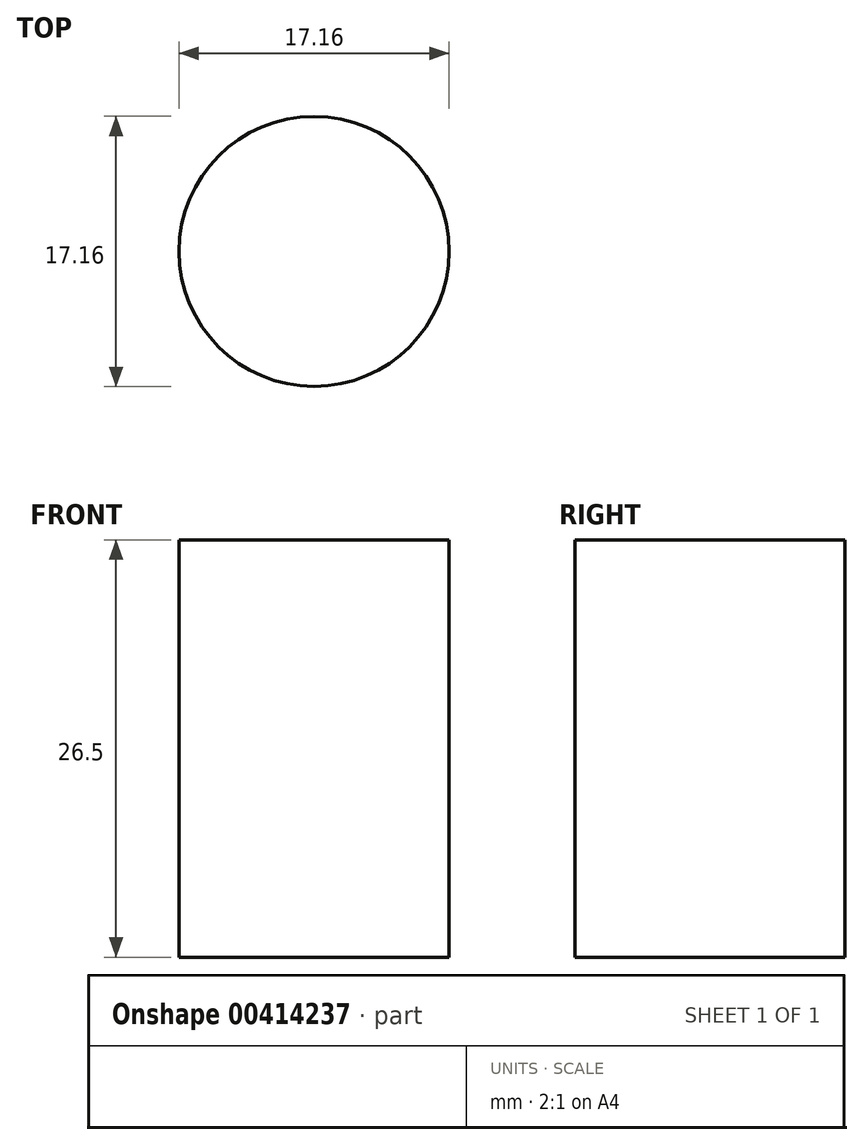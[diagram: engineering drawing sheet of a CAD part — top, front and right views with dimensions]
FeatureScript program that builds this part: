
annotation { "Feature Type Name" : "Feature", "Feature Type Description" : "" }
export const myFeature = defineFeature(function(context is Context, id is Id, definition is map)
    precondition{}
    {
        {
            var Q0;
            Q0=qCreatedBy(makeId("Top.planeOp"),FACE);
            var sketch = newSketch(context, id + "F0", { "sketchPlane" : qUnion([Q0])});
            skCircle(sketch, "E0", {"center": v(0, 0) * mm, "radius": 8.57 * mm});
            skSolve(sketch);
        }
        {
            var Q0;
            Q0 = qSketchRegion(id + "F0", true);
            extrude(context, id + "F1", {"entities" : qUnion([Q0]), "depth" : 26.5 * mm});
        }
    });
